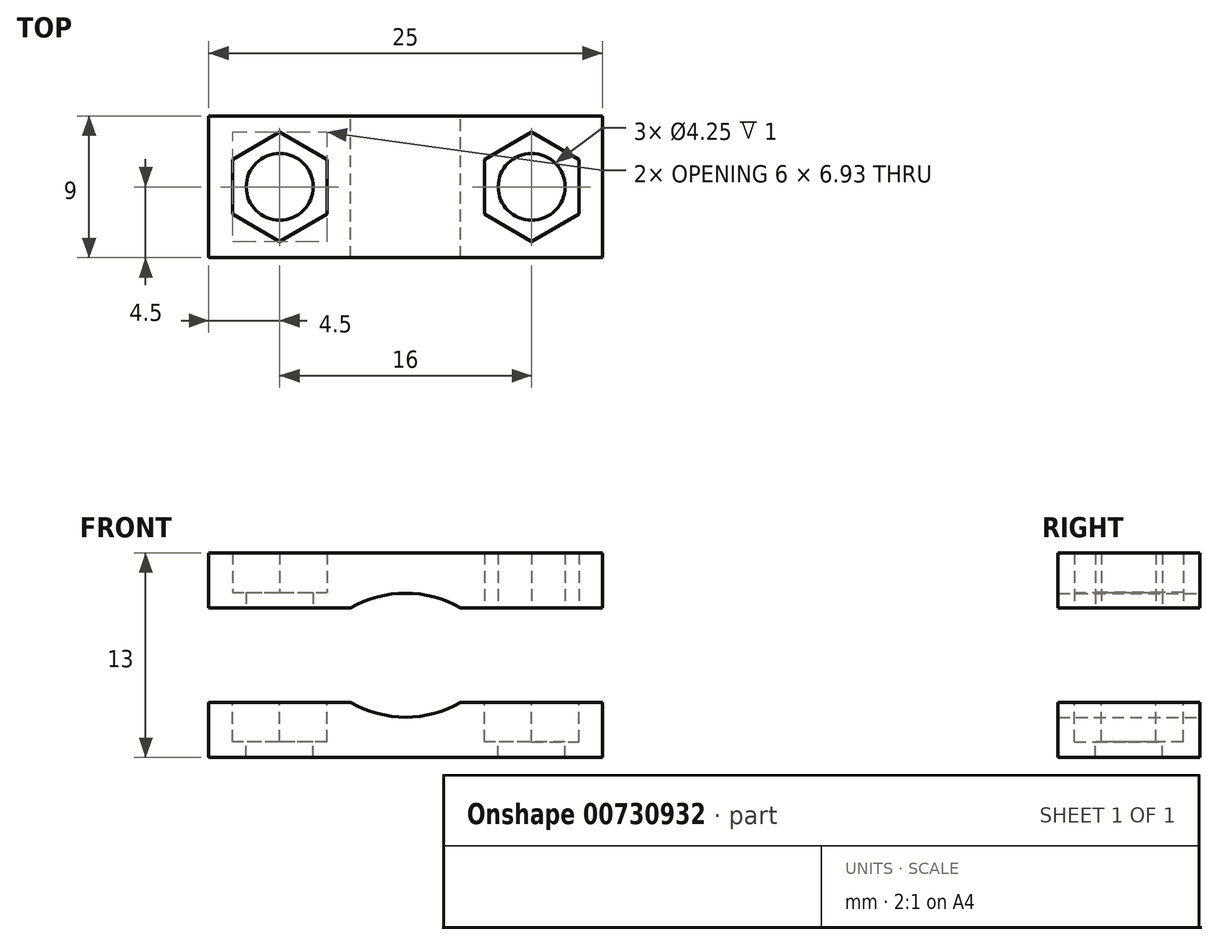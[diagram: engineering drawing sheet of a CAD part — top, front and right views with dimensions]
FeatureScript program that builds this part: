
annotation { "Feature Type Name" : "Feature", "Feature Type Description" : "" }
export const myFeature = defineFeature(function(context is Context, id is Id, definition is map)
    precondition{}
    {
        {
            var Q0;
            Q0=qCreatedBy(makeId("Front.planeOp"),FACE);
            var sketch = newSketch(context, id + "F0", { "sketchPlane" : qUnion([Q0])});
            skLineSegment(sketch, "E0.bottom", {"start": v(-3.5, 0.25) * mm, "end": v(3.5, 0.25) * mm});
            skLineSegment(sketch, "E0.top", {"start": v(-3.5, -0.25) * mm, "end": v(3.5, -0.25) * mm});
            skLineSegment(sketch, "E0.left", {"start": v(-3.5, 0.25) * mm, "end": v(-3.5, -0.25) * mm});
            skLineSegment(sketch, "E0.right", {"start": v(3.5, 0.25) * mm, "end": v(3.5, -0.25) * mm});
            skPoint(sketch, "E0.middle", {"position": v(0, 0) * mm});
            skLineSegment(sketch, "E1", {"start": v(-3.5, 0.25) * mm, "end": v(-3.5, 3.25) * mm});
            skLineSegment(sketch, "E2", {"start": v(3.5, 0.25) * mm, "end": v(3.5, 3.25) * mm});
            skArc(sketch, "E3", {"start": v(-3.5, 3.25) * mm, "mid": v(0, 2.31) * mm, "end": v(3.5, 3.25) * mm});
            skLineSegment(sketch, "E4", {"start": v(-3.5, 6.25) * mm, "end": v(3.5, 6.25) * mm, "construction": true});
            skLineSegment(sketch, "E5.bottom", {"start": v(-3.5, -0.25) * mm, "end": v(-12.5, -0.25) * mm});
            skLineSegment(sketch, "E5.top", {"start": v(-3.5, 3.25) * mm, "end": v(-12.5, 3.25) * mm});
            skLineSegment(sketch, "E5.left", {"start": v(-3.5, -0.25) * mm, "end": v(-3.5, 3.25) * mm});
            skLineSegment(sketch, "E5.right", {"start": v(-12.5, -0.25) * mm, "end": v(-12.5, 3.25) * mm});
            skLineSegment(sketch, "E6.bottom", {"start": v(3.5, -0.25) * mm, "end": v(12.5, -0.25) * mm});
            skLineSegment(sketch, "E6.top", {"start": v(3.5, 3.25) * mm, "end": v(12.5, 3.25) * mm});
            skLineSegment(sketch, "E6.left", {"start": v(3.5, -0.25) * mm, "end": v(3.5, 3.25) * mm});
            skLineSegment(sketch, "E6.right", {"start": v(12.5, -0.25) * mm, "end": v(12.5, 3.25) * mm});
            skLineSegment(sketch, "E7.MirrorCS", {"start": v(3.5, 12.25) * mm, "end": v(3.5, 12.75) * mm});
            skLineSegment(sketch, "E8.MirrorCS", {"start": v(-3.5, 12.25) * mm, "end": v(-3.5, 12.75) * mm});
            skLineSegment(sketch, "E9.MirrorCS", {"start": v(3.5, 12.75) * mm, "end": v(3.5, 9.25) * mm});
            skLineSegment(sketch, "E10.MirrorCS", {"start": v(-3.5, 12.75) * mm, "end": v(-3.5, 9.25) * mm});
            skLineSegment(sketch, "E11.MirrorCS", {"start": v(-3.5, 12.25) * mm, "end": v(3.5, 12.25) * mm});
            skPoint(sketch, "E12.MirrorP", {"position": v(0, 12.5) * mm});
            skLineSegment(sketch, "E13.MirrorCS", {"start": v(3.5, 12.25) * mm, "end": v(3.5, 9.25) * mm});
            skLineSegment(sketch, "E14.MirrorCS", {"start": v(-12.5, 12.75) * mm, "end": v(-12.5, 9.25) * mm});
            skLineSegment(sketch, "E15.MirrorCS", {"start": v(-3.5, 9.25) * mm, "end": v(-12.5, 9.25) * mm});
            skLineSegment(sketch, "E16.MirrorCS", {"start": v(12.5, 12.75) * mm, "end": v(12.5, 9.25) * mm});
            skArc(sketch, "E17.MirrorCS", {"start": v(-3.5, 9.25) * mm, "mid": v(0, 10.19) * mm, "end": v(3.5, 9.25) * mm});
            skLineSegment(sketch, "E18.MirrorCS", {"start": v(3.5, 9.25) * mm, "end": v(12.5, 9.25) * mm});
            skLineSegment(sketch, "E19.MirrorCS", {"start": v(-3.5, 12.25) * mm, "end": v(-3.5, 9.25) * mm});
            skLineSegment(sketch, "E20.MirrorCS", {"start": v(3.5, 12.75) * mm, "end": v(12.5, 12.75) * mm});
            skLineSegment(sketch, "E21.MirrorCS", {"start": v(-3.5, 12.75) * mm, "end": v(3.5, 12.75) * mm});
            skLineSegment(sketch, "E22.MirrorCS", {"start": v(-3.5, 12.75) * mm, "end": v(-12.5, 12.75) * mm});
            skSolve(sketch);
        }
        {
            var Q0;
            Q0 = qSketchRegion(id + "F0", true);
            extrude(context, id + "F1", {"entities" : qUnion([Q0]), "depth" : 9 * mm, "offsetDistance" : 25 * mm, "symmetric" : true});
        }
        {
            var Q0;
            Q0=makeQuery(id+"F1.opExtrude","SWEPT_FACE",FACE,{"disambiguationData":[OSD([sQuery(id+"F0.wireOp",EDGE,"E5.top")])]});
            var sketch = newSketch(context, id + "F2", { "sketchPlane" : qUnion([Q0])});
            skLineSegment(sketch, "E23", {"start": v(0, -5.51) * mm, "end": v(0, 5.58) * mm, "construction": true});
            skCircle(sketch, "E24.cCircle", {"center": v(-8, 0) * mm, "radius": 3 * mm, "construction": true});
            skPoint(sketch, "E24.cCircle.centerSnap0", {"position": v(-8, 4.5) * mm});
            skLineSegment(sketch, "E24.0", {"start": v(-8, -3.46) * mm, "end": v(-11, -1.73) * mm});
            skLineSegment(sketch, "E24.1", {"start": v(-11, -1.73) * mm, "end": v(-11, 1.73) * mm});
            skLineSegment(sketch, "E24.2", {"start": v(-11, 1.73) * mm, "end": v(-8, 3.46) * mm});
            skLineSegment(sketch, "E24.3", {"start": v(-8, 3.46) * mm, "end": v(-5, 1.73) * mm});
            skLineSegment(sketch, "E24.4", {"start": v(-5, 1.73) * mm, "end": v(-5, -1.73) * mm});
            skLineSegment(sketch, "E24.5", {"start": v(-5, -1.73) * mm, "end": v(-8, -3.46) * mm});
            skPoint(sketch, "E24.0.midPoint", {"position": v(-9.5, -2.6) * mm});
            skLineSegment(sketch, "E25.MirrorCS", {"start": v(5, -1.73) * mm, "end": v(8, -3.46) * mm});
            skLineSegment(sketch, "E26.MirrorCS", {"start": v(5, 1.73) * mm, "end": v(5, -1.73) * mm});
            skLineSegment(sketch, "E27.MirrorCS", {"start": v(8, -3.46) * mm, "end": v(11, -1.73) * mm});
            skPoint(sketch, "E28.MirrorP", {"position": v(9.5, -2.6) * mm});
            skLineSegment(sketch, "E29.MirrorCS", {"start": v(11, 1.73) * mm, "end": v(8, 3.46) * mm});
            skLineSegment(sketch, "E30.MirrorCS", {"start": v(8, 3.46) * mm, "end": v(5, 1.73) * mm});
            skLineSegment(sketch, "E31.MirrorCS", {"start": v(11, -1.73) * mm, "end": v(11, 1.73) * mm});
            skCircle(sketch, "E32.MirrorC", {"center": v(8, 0) * mm, "radius": 3 * mm, "construction": true});
            skCircle(sketch, "E33", {"center": v(-8, 0) * mm, "radius": 2.12 * mm});
            skCircle(sketch, "E34", {"center": v(8, 0) * mm, "radius": 2.12 * mm});
            skSolve(sketch);
        }
        {
            var Q0;
            Q0=makeQuery(id+"F2.imprint","IMPRINT",FACE,{"disambiguationData":[TD([[makeQuery(id+"F2.imprint","IMPRINT",EDGE,{"derivedFrom":sQuery(id+"F2.wireOp",EDGE,"E24.0")}),-1.0]])]});
            var Q1;
            Q1=makeQuery(id+"F2.imprint","IMPRINT",FACE,{"disambiguationData":[TD([[makeQuery(id+"F2.imprint","IMPRINT",EDGE,{"derivedFrom":sQuery(id+"F2.wireOp",EDGE,"E25.MirrorCS")}),1.0]])]});
            extrude(context, id + "F3", {"entities" : qUnion([Q0, Q1]), "operationType" : NewBodyOperationType.REMOVE, "oppositeDirection" : true, "depth" : 2.5 * mm, "offsetDistance" : 25 * mm});
        }
        {
            var Q0;
            Q0=makeQuery(id+"F3.boolean.opBoolean","SPLIT",FACE,{"disambiguationData":[TD([makeQuery(id+"F3.opExtrude","SWEPT_FACE",FACE,{"disambiguationData":[OSD([sQuery(id+"F2.wireOp",EDGE,"E33")])]})])],"derivedFrom":makeQuery(id+"F1.opExtrude","SWEPT_FACE",FACE,{"disambiguationData":[OSD([sQuery(id+"F0.wireOp",EDGE,"E5.top")])]})});
            var Q1;
            Q1=makeQuery(id+"F3.boolean.opBoolean","SPLIT",FACE,{"disambiguationData":[TD([makeQuery(id+"F3.opExtrude","SWEPT_FACE",FACE,{"disambiguationData":[OSD([sQuery(id+"F2.wireOp",EDGE,"E34")])]})])],"derivedFrom":makeQuery(id+"F1.opExtrude","SWEPT_FACE",FACE,{"disambiguationData":[OSD([sQuery(id+"F0.wireOp",EDGE,"E6.top")])]})});
            var Q2;
            Q2=makeQuery(id+"F1.opExtrude","SWEPT_FACE",FACE,{"disambiguationData":[OSD([sQuery(id+"F0.wireOp",EDGE,"E0.top"),sQuery(id+"F0.wireOp",EDGE,"E5.bottom"),sQuery(id+"F0.wireOp",EDGE,"E6.bottom")])]});
            extrude(context, id + "F4", {"entities" : qUnion([Q0, Q1]), "operationType" : NewBodyOperationType.REMOVE, "endBound" : BoundingType.UP_TO_SURFACE, "oppositeDirection" : true, "depth" : 25 * mm, "endBoundEntityFace" : qUnion([Q2]), "offsetDistance" : 25 * mm});
        }
        {
            var Q0;
            Q0=makeQuery(id+"F1.opExtrude","SWEPT_FACE",FACE,{"disambiguationData":[OSD([sQuery(id+"F0.wireOp",EDGE,"E15.MirrorCS")])]});
            var sketch = newSketch(context, id + "F5", { "sketchPlane" : qUnion([Q0])});
            skCircle(sketch, "E35.cCircle", {"center": v(-8, 0) * mm, "radius": 3 * mm, "construction": true});
            skPoint(sketch, "E35.cCircle.centerSnap0", {"position": v(-8, 4.5) * mm});
            skLineSegment(sketch, "E35.0", {"start": v(-5, 1.73) * mm, "end": v(-5, -1.73) * mm});
            skLineSegment(sketch, "E35.1", {"start": v(-5, -1.73) * mm, "end": v(-8, -3.46) * mm});
            skLineSegment(sketch, "E35.2", {"start": v(-8, -3.46) * mm, "end": v(-11, -1.73) * mm});
            skLineSegment(sketch, "E35.3", {"start": v(-11, -1.73) * mm, "end": v(-11, 1.73) * mm});
            skLineSegment(sketch, "E35.4", {"start": v(-11, 1.73) * mm, "end": v(-8, 3.46) * mm});
            skLineSegment(sketch, "E35.5", {"start": v(-8, 3.46) * mm, "end": v(-5, 1.73) * mm});
            skPoint(sketch, "E35.0.midPoint", {"position": v(-5, 0) * mm});
            skCircle(sketch, "E36", {"center": v(-8, 0) * mm, "radius": 2.12 * mm});
            skLineSegment(sketch, "E37", {"start": v(0, 5) * mm, "end": v(0, -4.88) * mm, "construction": true});
            skLineSegment(sketch, "E38.MirrorCS", {"start": v(11, 1.73) * mm, "end": v(8, 3.46) * mm});
            skLineSegment(sketch, "E39.MirrorCS", {"start": v(8, -3.46) * mm, "end": v(11, -1.73) * mm});
            skLineSegment(sketch, "E40.MirrorCS", {"start": v(5, -1.73) * mm, "end": v(8, -3.46) * mm});
            skLineSegment(sketch, "E41.MirrorCS", {"start": v(8, 3.46) * mm, "end": v(5, 1.73) * mm});
            skCircle(sketch, "E42.MirrorC", {"center": v(8, 0) * mm, "radius": 3 * mm, "construction": true});
            skLineSegment(sketch, "E43.MirrorCS", {"start": v(5, 1.73) * mm, "end": v(5, -1.73) * mm});
            skCircle(sketch, "E44.MirrorC", {"center": v(8, 0) * mm, "radius": 2.12 * mm});
            skPoint(sketch, "E45.MirrorP", {"position": v(5, 0) * mm});
            skLineSegment(sketch, "E46.MirrorCS", {"start": v(11, -1.73) * mm, "end": v(11, 1.73) * mm});
            skSolve(sketch);
        }
        {
            var Q0;
            Q0=makeQuery(id+"F5.imprint","IMPRINT",FACE,{"disambiguationData":[TD([[makeQuery(id+"F5.imprint","IMPRINT",EDGE,{"derivedFrom":sQuery(id+"F5.wireOp",EDGE,"E36")}),1.0]])]});
            var Q1;
            Q1=makeQuery(id+"F5.imprint","IMPRINT",FACE,{"disambiguationData":[TD([[makeQuery(id+"F5.imprint","IMPRINT",EDGE,{"derivedFrom":sQuery(id+"F5.wireOp",EDGE,"E44.MirrorC")}),-1.0]])]});
            var Q2;
            Q2=makeQuery(id+"F1.opExtrude","SWEPT_FACE",FACE,{"disambiguationData":[OSD([sQuery(id+"F0.wireOp",EDGE,"E20.MirrorCS"),sQuery(id+"F0.wireOp",EDGE,"E21.MirrorCS"),sQuery(id+"F0.wireOp",EDGE,"E22.MirrorCS")])]});
            extrude(context, id + "F6", {"entities" : qUnion([Q0, Q1]), "operationType" : NewBodyOperationType.REMOVE, "endBound" : BoundingType.UP_TO_SURFACE, "oppositeDirection" : true, "depth" : 25 * mm, "endBoundEntityFace" : qUnion([Q2]), "offsetDistance" : 25 * mm});
        }
        {
            var Q0;
            Q0=makeQuery(id+"F5.imprint","IMPRINT",FACE,{"disambiguationData":[TD([[makeQuery(id+"F5.imprint","IMPRINT",EDGE,{"derivedFrom":sQuery(id+"F5.wireOp",EDGE,"E35.0")}),-1.0]])]});
            var Q1;
            Q1=makeQuery(id+"F5.imprint","IMPRINT",FACE,{"disambiguationData":[TD([[makeQuery(id+"F5.imprint","IMPRINT",EDGE,{"derivedFrom":sQuery(id+"F5.wireOp",EDGE,"E38.MirrorCS")}),1.0]])]});
            var Q2;
            Q2=makeQuery(id+"F1.opExtrude","SWEPT_FACE",FACE,{"disambiguationData":[OSD([sQuery(id+"F0.wireOp",EDGE,"E20.MirrorCS"),sQuery(id+"F0.wireOp",EDGE,"E21.MirrorCS"),sQuery(id+"F0.wireOp",EDGE,"E22.MirrorCS")])]});
            extrude(context, id + "F7", {"entities" : qUnion([Q0, Q1]), "operationType" : NewBodyOperationType.REMOVE, "endBound" : BoundingType.UP_TO_SURFACE, "oppositeDirection" : true, "depth" : 25 * mm, "endBoundEntityFace" : qUnion([Q2]), "offsetDistance" : 1 * mm, "hasSecondDirection" : true, "secondDirectionOppositeDirection" : true, "secondDirectionDepth" : 1 * mm});
        }
    });
